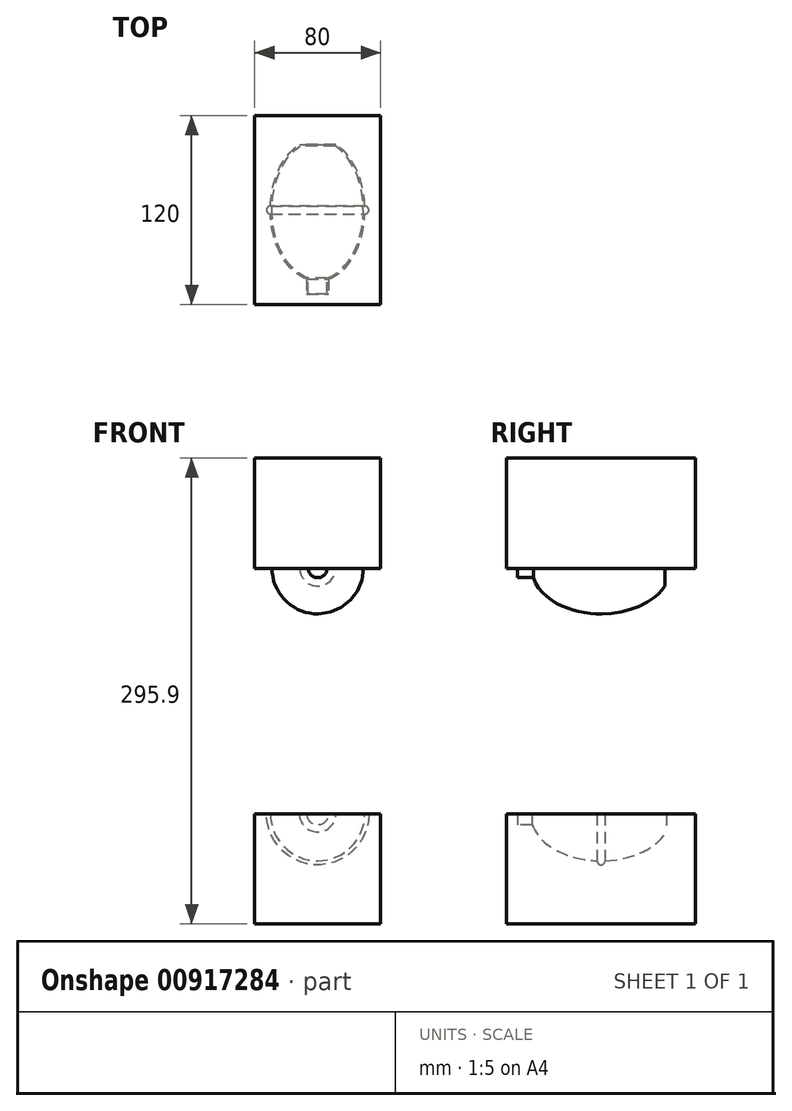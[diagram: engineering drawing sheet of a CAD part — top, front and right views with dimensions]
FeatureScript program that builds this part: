
annotation { "Feature Type Name" : "Feature", "Feature Type Description" : "" }
export const myFeature = defineFeature(function(context is Context, id is Id, definition is map)
    precondition{}
    {
        {
            var Q0;
            Q0=qCreatedBy(makeId("Top.planeOp"),FACE);
            var sketch = newSketch(context, id + "F0", { "sketchPlane" : qUnion([Q0])});
            skLineSegment(sketch, "E0.bottom", {"start": v(40, -60) * mm, "end": v(-40, -60) * mm});
            skLineSegment(sketch, "E0.top", {"start": v(40, 60) * mm, "end": v(-40, 60) * mm});
            skLineSegment(sketch, "E0.left", {"start": v(40, -60) * mm, "end": v(40, 60) * mm});
            skLineSegment(sketch, "E0.right", {"start": v(-40, -60) * mm, "end": v(-40, 60) * mm});
            skPoint(sketch, "E0.middle", {"position": v(0, 0) * mm});
            skEllipse(sketch, "E1", {"center": v(0, 0) * mm, "majorRadius": 45 * mm, "minorRadius": 30 * mm, "majorAxis": v(0, -1)});
            skLineSegment(sketch, "E2.bottom", {"start": v(7, 36.8) * mm, "end": v(-7, 36.8) * mm});
            skLineSegment(sketch, "E2.top", {"start": v(7, 53.2) * mm, "end": v(-7, 53.2) * mm});
            skLineSegment(sketch, "E2.left", {"start": v(7, 36.8) * mm, "end": v(7, 53.2) * mm});
            skLineSegment(sketch, "E2.right", {"start": v(-7, 36.8) * mm, "end": v(-7, 53.2) * mm});
            skPoint(sketch, "E2.middle", {"position": v(0, 45) * mm});
            skLineSegment(sketch, "E3.bottom", {"start": v(20, -48.5) * mm, "end": v(-20, -48.5) * mm});
            skLineSegment(sketch, "E3.top", {"start": v(20, -41.5) * mm, "end": v(-20, -41.5) * mm});
            skLineSegment(sketch, "E3.left", {"start": v(20, -48.5) * mm, "end": v(20, -41.5) * mm});
            skLineSegment(sketch, "E3.right", {"start": v(-20, -48.5) * mm, "end": v(-20, -41.5) * mm});
            skPoint(sketch, "E3.middle", {"position": v(0, -45) * mm});
            skCircle(sketch, "E4", {"center": v(-30, 0) * mm, "radius": 2.5 * mm});
            skLineSegment(sketch, "E5", {"start": v(0, -45) * mm, "end": v(0, 53.2) * mm});
            skSolve(sketch);
        }
        {
            var Q0;
            Q0=qCreatedBy(makeId("Top.planeOp"),FACE);
            var sketch = newSketch(context, id + "F1", { "sketchPlane" : qUnion([Q0])});
            skSolve(sketch);
        }
        {
            var Q0;
            Q0 = qSketchRegion(id + "F1", true);
            var Q1;
            Q1=makeQuery(id+"F0.imprint","IMPRINT",FACE,{"disambiguationData":[TD([[makeQuery(id+"F0.imprint","IMPRINT",EDGE,{"derivedFrom":sQuery(id+"F0.wireOp",EDGE,"E0.bottom")}),-1.0]])]});
            var Q2;
            {var subQ0=sQuery(id+"F0.wireOp",EDGE,"E2.bottom");Q2=makeQuery(id+"F0.imprint","IMPRINT",FACE,{"disambiguationData":[TD([[makeQuery(id+"F0.imprint","IMPRINT",EDGE,{"derivedFrom":subQ0}),1.0]])]});}
            var Q3;
            {var subQ5=sQuery(id+"F0.wireOp",EDGE,"E2.bottom");Q3=makeQuery(id+"F0.imprint","IMPRINT",FACE,{"disambiguationData":[TD([[makeQuery(id+"F0.imprint","IMPRINT",EDGE,{"derivedFrom":subQ5}),-1.0]])]});}
            var Q4;
            {var subQ5=sQuery(id+"F0.wireOp",EDGE,"E2.top");Q4=makeQuery(id+"F0.imprint","IMPRINT",FACE,{"disambiguationData":[TD([[makeQuery(id+"F0.imprint","IMPRINT",EDGE,{"derivedFrom":subQ5}),1.0]])]});}
            var Q5;
            {var subQ0=sQuery(id+"F0.wireOp",EDGE,"E4");var subQ1=sQuery(id+"F0.wireOp",EDGE,"E1");var subQ2=makeQuery(id+"F0.imprint","INTERSECT",VERTEX,{"disambiguationData":[OD(0.0)],"derivedFrom":[subQ1,subQ0]});Q5=makeQuery(id+"F0.imprint","IMPRINT",FACE,{"disambiguationData":[TD([[makeQuery(id+"F0.imprint","IMPRINT",EDGE,{"disambiguationData":[TD([[subQ2,-1.0]])],"derivedFrom":subQ1}),-1.0]])]});}
            var Q6;
            {var subQ0=sQuery(id+"F0.wireOp",EDGE,"E4");var subQ1=sQuery(id+"F0.wireOp",EDGE,"E1");var subQ2=makeQuery(id+"F0.imprint","INTERSECT",VERTEX,{"disambiguationData":[OD(0.0)],"derivedFrom":[subQ1,subQ0]});Q6=makeQuery(id+"F0.imprint","IMPRINT",FACE,{"disambiguationData":[TD([[makeQuery(id+"F0.imprint","IMPRINT",EDGE,{"disambiguationData":[TD([[subQ2,-1.0]])],"derivedFrom":subQ1}),1.0]])]});}
            var Q7;
            {var subQ0=sQuery(id+"F0.wireOp",EDGE,"E3.top");var subQ1=sQuery(id+"F0.wireOp",EDGE,"E1");var subQ2=makeQuery(id+"F0.imprint","INTERSECT",VERTEX,{"disambiguationData":[OD(0.0)],"derivedFrom":[subQ1,subQ0]});Q7=makeQuery(id+"F0.imprint","IMPRINT",FACE,{"disambiguationData":[TD([[makeQuery(id+"F0.imprint","IMPRINT",EDGE,{"disambiguationData":[TD([[subQ2,1.0]])],"derivedFrom":subQ1}),1.0]])]});}
            var Q8;
            Q8=makeQuery(id+"F0.imprint","IMPRINT",FACE,{"disambiguationData":[TD([[makeQuery(id+"F0.imprint","IMPRINT",EDGE,{"derivedFrom":sQuery(id+"F0.wireOp",EDGE,"E3.bottom")}),-1.0]])]});
            var Q9;
            {var subQ1=sQuery(id+"F0.wireOp",EDGE,"E1");var subQ5=sQuery(id+"F0.wireOp",EDGE,"E2.right");var subQ8=makeQuery(id+"F0.imprint","INTERSECT",VERTEX,{"derivedFrom":[subQ1,subQ5]});Q9=makeQuery(id+"F0.imprint","IMPRINT",FACE,{"disambiguationData":[TD([[makeQuery(id+"F0.imprint","IMPRINT",EDGE,{"disambiguationData":[TD([[subQ8,-1.0]])],"derivedFrom":subQ1}),1.0]])]});}
            var Q10;
            {var subQ0=sQuery(id+"F0.wireOp",EDGE,"E5");var subQ1=sQuery(id+"F0.wireOp",EDGE,"E1");var subQ2=makeQuery(id+"F0.imprint","INTERSECT",VERTEX,{"disambiguationData":[OD(0.0)],"derivedFrom":[subQ1,subQ0]});Q10=makeQuery(id+"F0.imprint","IMPRINT",FACE,{"disambiguationData":[TD([[makeQuery(id+"F0.imprint","IMPRINT",EDGE,{"disambiguationData":[TD([[subQ2,1.0]])],"derivedFrom":subQ1}),1.0]])]});}
            extrude(context, id + "F2", {"entities" : qUnion([Q0, Q1, Q2, Q3, Q4, Q5, Q6, Q7, Q8, Q9, Q10]), "depth" : 70 * mm, "offsetDistance" : 25 * mm});
        }
        {
            var Q0;
            Q0=makeQuery(id+"F2.opExtrude","SWEPT_BODY",BODY,{"disambiguationData":[OSD([sQuery(id+"F0.wireOp",EDGE,"E0.bottom"),sQuery(id+"F0.wireOp",EDGE,"E0.top"),sQuery(id+"F0.wireOp",EDGE,"E0.left"),sQuery(id+"F0.wireOp",EDGE,"E0.right")])]});
            transform(context, id + "F3", {"entities" : qUnion([Q0]), "transformType" : TransformType.TRANSLATION_3D, "dx" : 0 * mm, "dy" : 0 * mm, "dz" : 155.9 * mm, "makeCopy" : true});
        }
        {
            var Q0;
            {var subQ1=sQuery(id+"F0.wireOp",EDGE,"E1");var subQ5=sQuery(id+"F0.wireOp",EDGE,"E2.right");var subQ8=makeQuery(id+"F0.imprint","INTERSECT",VERTEX,{"derivedFrom":[subQ1,subQ5]});Q0=makeQuery(id+"F0.imprint","IMPRINT",FACE,{"disambiguationData":[TD([[makeQuery(id+"F0.imprint","IMPRINT",EDGE,{"disambiguationData":[TD([[subQ8,-1.0]])],"derivedFrom":subQ1}),1.0]])]});}
            var Q1;
            {var subQ0=sQuery(id+"F0.wireOp",EDGE,"E4");var subQ1=sQuery(id+"F0.wireOp",EDGE,"E1");var subQ2=makeQuery(id+"F0.imprint","INTERSECT",VERTEX,{"disambiguationData":[OD(0.0)],"derivedFrom":[subQ1,subQ0]});Q1=makeQuery(id+"F0.imprint","IMPRINT",FACE,{"disambiguationData":[TD([[makeQuery(id+"F0.imprint","IMPRINT",EDGE,{"disambiguationData":[TD([[subQ2,-1.0]])],"derivedFrom":subQ1}),1.0]])]});}
            var Q2;
            {var subQ0=sQuery(id+"F0.wireOp",EDGE,"E4");var subQ1=sQuery(id+"F0.wireOp",EDGE,"E1");var subQ2=makeQuery(id+"F0.imprint","INTERSECT",VERTEX,{"disambiguationData":[OD(0.0)],"derivedFrom":[subQ1,subQ0]});Q2=makeQuery(id+"F0.imprint","IMPRINT",FACE,{"disambiguationData":[TD([[makeQuery(id+"F0.imprint","IMPRINT",EDGE,{"disambiguationData":[TD([[subQ2,-1.0]])],"derivedFrom":subQ1}),-1.0]])]});}
            var Q3;
            {var subQ0=sQuery(id+"F0.wireOp",EDGE,"E5");var subQ1=sQuery(id+"F0.wireOp",EDGE,"E1");var subQ2=makeQuery(id+"F0.imprint","INTERSECT",VERTEX,{"disambiguationData":[OD(1.0)],"derivedFrom":[subQ1,subQ0]});Q3=makeQuery(id+"F0.imprint","IMPRINT",FACE,{"disambiguationData":[TD([[makeQuery(id+"F0.imprint","IMPRINT",EDGE,{"disambiguationData":[TD([[subQ2,-1.0]])],"derivedFrom":subQ1}),1.0]])]});}
            var Q4;
            {var subQ0=sQuery(id+"F0.wireOp",EDGE,"E5");var subQ1=sQuery(id+"F0.wireOp",EDGE,"E1");var subQ2=makeQuery(id+"F0.imprint","INTERSECT",VERTEX,{"disambiguationData":[OD(1.0)],"derivedFrom":[subQ1,subQ0]});Q4=makeQuery(id+"F0.imprint","IMPRINT",FACE,{"disambiguationData":[TD([[makeQuery(id+"F0.imprint","IMPRINT",EDGE,{"disambiguationData":[TD([[subQ2,-1.0]])],"derivedFrom":subQ1}),-1.0]])]});}
            var Q5;
            Q5=sQuery(id+"F0.wireOp",EDGE,"E5");
            revolve(context, id + "F4", {"operationType" : NewBodyOperationType.REMOVE, "surfaceOperationType" : NewSurfaceOperationType.NEW, "entities" : qUnion([Q0, Q1, Q2, Q3, Q4]), "axis" : qUnion([Q5]), "revolveType" : RevolveType.FULL, "oppositeDirection" : true});
        }
        {
            var Q0;
            Q0=makeQuery(id+"F3.opPattern","COPY",FACE,{"derivedFrom":makeQuery(id+"F2.opExtrude","CAP_FACE",FACE,{"disambiguationData":[OSD([sQuery(id+"F0.wireOp",EDGE,"E0.bottom"),sQuery(id+"F0.wireOp",EDGE,"E0.top"),sQuery(id+"F0.wireOp",EDGE,"E0.left"),sQuery(id+"F0.wireOp",EDGE,"E0.right")])],"isStart":true}),"instanceName":"1"});
            var sketch = newSketch(context, id + "F5", { "sketchPlane" : qUnion([Q0])});
            skLineSegment(sketch, "E6.bottom", {"start": v(40, -60) * mm, "end": v(-40, -60) * mm});
            skLineSegment(sketch, "E6.top", {"start": v(40, 60) * mm, "end": v(-40, 60) * mm});
            skLineSegment(sketch, "E6.left", {"start": v(40, -60) * mm, "end": v(40, 60) * mm});
            skLineSegment(sketch, "E6.right", {"start": v(-40, -60) * mm, "end": v(-40, 60) * mm});
            skPoint(sketch, "E6.middle", {"position": v(0, 0) * mm});
            skEllipse(sketch, "E7", {"center": v(0, 0) * mm, "majorRadius": 44 * mm, "minorRadius": 29 * mm, "majorAxis": v(0, -1)});
            skLineSegment(sketch, "E8.bottom", {"start": v(6, 34.8) * mm, "end": v(-6, 34.8) * mm});
            skLineSegment(sketch, "E8.top", {"start": v(6, 53.2) * mm, "end": v(-6, 53.2) * mm});
            skLineSegment(sketch, "E8.left", {"start": v(6, 34.8) * mm, "end": v(6, 53.2) * mm});
            skLineSegment(sketch, "E8.right", {"start": v(-6, 34.8) * mm, "end": v(-6, 53.2) * mm});
            skPoint(sketch, "E8.middle", {"position": v(0, 44) * mm});
            skLineSegment(sketch, "E9.bottom", {"start": v(20, -47.5) * mm, "end": v(-20, -47.5) * mm});
            skLineSegment(sketch, "E9.top", {"start": v(20, -40.5) * mm, "end": v(-20, -40.5) * mm});
            skLineSegment(sketch, "E9.left", {"start": v(20, -47.5) * mm, "end": v(20, -40.5) * mm});
            skLineSegment(sketch, "E9.right", {"start": v(-20, -47.5) * mm, "end": v(-20, -40.5) * mm});
            skPoint(sketch, "E9.middle", {"position": v(0, -44) * mm});
            skLineSegment(sketch, "E10", {"start": v(0, -44) * mm, "end": v(0, 53.2) * mm});
            skPoint(sketch, "E11", {"position": v(-6, 43.05) * mm});
            skPoint(sketch, "E12", {"position": v(6, 43.05) * mm});
            skSolve(sketch);
        }
        {
            var Q0;
            {var subQ0=sQuery(id+"F5.wireOp",EDGE,"51bbd463-7ca7-4629-ac05-9dc961f02058");var subQ1=sQuery(id+"F5.wireOp",EDGE,"E7");var subQ2=makeQuery(id+"F5.imprint","INTERSECT",VERTEX,{"disambiguationData":[OD(0.0)],"derivedFrom":[subQ1,subQ0]});Q0=makeQuery(id+"F5.imprint","IMPRINT",FACE,{"disambiguationData":[TD([[makeQuery(id+"F5.imprint","IMPRINT",EDGE,{"disambiguationData":[TD([[subQ2,-1.0]])],"derivedFrom":subQ1}),-1.0]])]});}
            var Q1;
            {var subQ0=sQuery(id+"F5.wireOp",EDGE,"51bbd463-7ca7-4629-ac05-9dc961f02058");var subQ1=sQuery(id+"F5.wireOp",EDGE,"E7");var subQ2=makeQuery(id+"F5.imprint","INTERSECT",VERTEX,{"disambiguationData":[OD(0.0)],"derivedFrom":[subQ1,subQ0]});Q1=makeQuery(id+"F5.imprint","IMPRINT",FACE,{"disambiguationData":[TD([[makeQuery(id+"F5.imprint","IMPRINT",EDGE,{"disambiguationData":[TD([[subQ2,-1.0]])],"derivedFrom":subQ1}),1.0]])]});}
            var Q2;
            {var subQ1=sQuery(id+"F5.wireOp",EDGE,"E7");var subQ5=sQuery(id+"F5.wireOp",EDGE,"E8.right");var subQ8=makeQuery(id+"F5.imprint","INTERSECT",VERTEX,{"derivedFrom":[subQ1,subQ5]});Q2=makeQuery(id+"F5.imprint","IMPRINT",FACE,{"disambiguationData":[TD([[makeQuery(id+"F5.imprint","IMPRINT",EDGE,{"disambiguationData":[TD([[subQ8,-1.0]])],"derivedFrom":subQ1}),1.0]])]});}
            var Q3;
            {var subQ0=sQuery(id+"F5.wireOp",EDGE,"E10");var subQ1=sQuery(id+"F5.wireOp",EDGE,"E7");var subQ2=makeQuery(id+"F5.imprint","INTERSECT",VERTEX,{"disambiguationData":[OD(1.0)],"derivedFrom":[subQ1,subQ0]});Q3=makeQuery(id+"F5.imprint","IMPRINT",FACE,{"disambiguationData":[TD([[makeQuery(id+"F5.imprint","IMPRINT",EDGE,{"disambiguationData":[TD([[subQ2,-1.0]])],"derivedFrom":subQ1}),1.0]])]});}
            var Q4;
            {var subQ0=sQuery(id+"F5.wireOp",EDGE,"E10");var subQ1=sQuery(id+"F5.wireOp",EDGE,"E7");var subQ2=makeQuery(id+"F5.imprint","INTERSECT",VERTEX,{"disambiguationData":[OD(1.0)],"derivedFrom":[subQ1,subQ0]});Q4=makeQuery(id+"F5.imprint","IMPRINT",FACE,{"disambiguationData":[TD([[makeQuery(id+"F5.imprint","IMPRINT",EDGE,{"disambiguationData":[TD([[subQ2,-1.0]])],"derivedFrom":subQ1}),-1.0]])]});}
            var Q5;
            Q5=sQuery(id+"F5.wireOp",EDGE,"E10");
            revolve(context, id + "F6", {"operationType" : NewBodyOperationType.ADD, "surfaceOperationType" : NewSurfaceOperationType.NEW, "entities" : qUnion([Q0, Q1, Q2, Q3, Q4]), "axis" : qUnion([Q5]), "revolveType" : RevolveType.FULL});
        }
        {
            var Q0;
            Q0=qCreatedBy(makeId("Top.planeOp"),FACE);
            var sketch = newSketch(context, id + "F7", { "sketchPlane" : qUnion([Q0])});
            skLineSegment(sketch, "E13", {"start": v(-40.6, 0) * mm, "end": v(41.08, 0) * mm});
            skSolve(sketch);
        }
        {
            var Q0;
            Q0=makeQuery(id+"F2.opExtrude","SWEPT_BODY",BODY,{"disambiguationData":[OSD([sQuery(id+"F0.wireOp",EDGE,"E0.bottom"),sQuery(id+"F0.wireOp",EDGE,"E0.top"),sQuery(id+"F0.wireOp",EDGE,"E0.left"),sQuery(id+"F0.wireOp",EDGE,"E0.right")])]});
            var Q1;
            Q1=sQuery(id+"F7.wireOp",EDGE,"E13");
            var Q2;
            Q2=sQuery(id+"F7.wireOp",EDGE,"E13");
            transform(context, id + "F8", {"entities" : qUnion([Q0]), "transformType" : TransformType.ROTATION, "transformAxis" : qUnion([Q2]), "angle" : 180 * degree, "makeCopy" : false});
        }
    });
